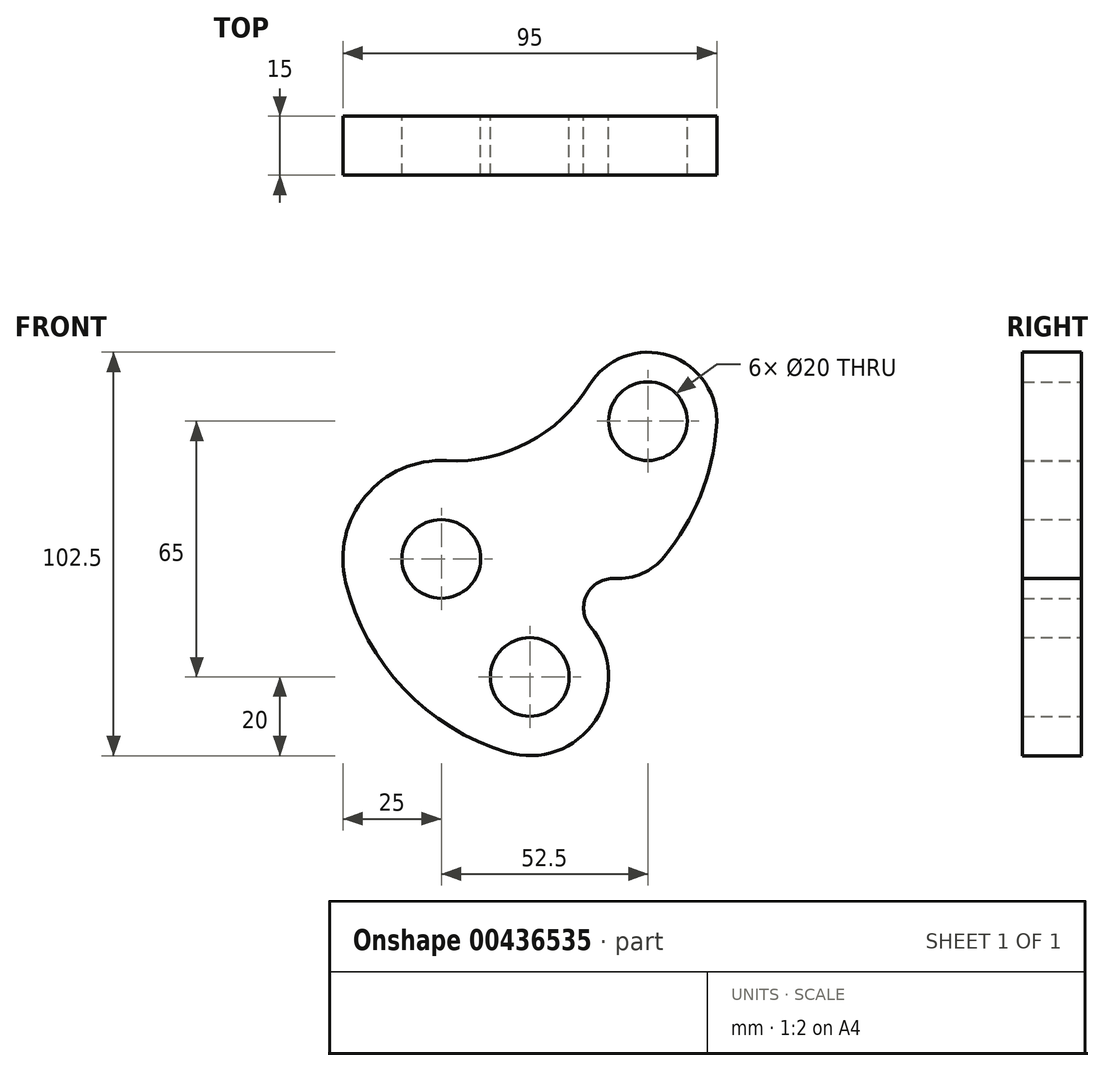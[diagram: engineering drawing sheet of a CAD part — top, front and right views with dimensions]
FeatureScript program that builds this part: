
annotation { "Feature Type Name" : "Feature", "Feature Type Description" : "" }
export const myFeature = defineFeature(function(context is Context, id is Id, definition is map)
    precondition{}
    {
        {
            var Q0;
            Q0=qCreatedBy(makeId("Front.planeOp"),FACE);
            var sketch = newSketch(context, id + "F0", { "sketchPlane" : qUnion([Q0])});
            skCircle(sketch, "E0", {"center": v(0, 0) * mm, "radius": 10 * mm});
            skCircle(sketch, "E1", {"center": v(22.5, -30) * mm, "radius": 10 * mm});
            skCircle(sketch, "E2", {"center": v(52.5, 35) * mm, "radius": 10 * mm});
            skArc(sketch, "E3", {"start": v(37.55, 44.1) * mm, "mid": v(57.9, 51.64) * mm, "end": v(69.94, 33.58) * mm});
            skArc(sketch, "E4", {"start": v(37.9, -17.24) * mm, "mid": v(39.17, -41.05) * mm, "end": v(16.75, -49.16) * mm});
            skArc(sketch, "E5", {"start": v(1.3, 24.97) * mm, "mid": v(-19.26, 15.94) * mm, "end": v(-24.28, -5.94) * mm});
            skArc(sketch, "E6", {"start": v(-24.28, -5.94) * mm, "mid": v(-9.51, -33) * mm, "end": v(16.75, -49.16) * mm});
            skArc(sketch, "E7", {"start": v(1.3, 24.97) * mm, "mid": v(22.07, 29.54) * mm, "end": v(37.55, 44.1) * mm});
            skArc(sketch, "E8", {"start": v(56.62, 0.51) * mm, "mid": v(51.03, -3.73) * mm, "end": v(44.12, -4.97) * mm});
            skArc(sketch, "E9", {"start": v(56.62, 0.51) * mm, "mid": v(65.8, 16.03) * mm, "end": v(69.94, 33.58) * mm});
            skArc(sketch, "E10", {"start": v(44.12, -4.97) * mm, "mid": v(37, -9.07) * mm, "end": v(37.9, -17.24) * mm});
            skSolve(sketch);
        }
        {
            var Q0;
            Q0=makeQuery(id+"F0.imprint","IMPRINT",FACE,{"disambiguationData":[TD([[makeQuery(id+"F0.imprint","IMPRINT",EDGE,{"derivedFrom":sQuery(id+"F0.wireOp",EDGE,"E0")}),-1.0]])]});
            extrude(context, id + "F1", {"entities" : qUnion([Q0]), "depth" : 15 * mm});
        }
    });
